# Revit family: Sink-Top_Mount-Kitchen-KOHLER-Purist-K-28408T_1
name_source: partatom
category: Plumbing Fixtures
units: mm (PartAtom-declared; Revit-internal decimal feet)

## family parameters
Cut with Voids When Loaded = No
Host = Face
OmniClass Number = 23.31.13.00
OmniClass Title = Sinks
Part Type = Normal
Room Calculation Point = No
Round Connector Dimension = Use Diameter
Shared = No

## types (1)
- NA-Stainless
    ADA Compliant = No
    Assembly Code = D2010400
    CW Connection = Yes
    Cold Water Inlet = Cold Water Inlet
    Date Modified = 12/13/2023
    Default Elevation = 36"
    Description = Purist Liquid Metal Sink & Atom Pull Down Kitchen Faucet
    Drain Included = Yes
    Finish = Kohler-Metal-NA-Stainless
    Flow Rate = 2 GPM
    HW Connection = Yes
    Handle Clearance = 2 15/16"
    Height = 28"
    Hot Water Inlet = Hot Water Inlet
    Length = 33 1/16"
    Manufacturer = Kohler Co.
    Master Format 2014 = 22 41 16
    Master Format 2014 Name = Residential Lavatories and Sinks
    Material = Stainless Steel
    Model = K-28408T-2ED-NA
    Pressure = 60.00 psi
    Product Name = Purist
    Spout Reach = 8 3/8"
    Type = 1
    URL = http://www.kohler.com.cn
    Vent Connection = No
    Waste Connection = Yes
    Waste Water Outlet 2 = Waste Water Outlet 2
    Waste water Outlet 1 = Waste water Outlet 1
    WaterSense Certified = No
    Width = 18 1/2"

## geometry (parser evidence)
native form markers: Sweep x11
no freeform markers — native parametric forms only
